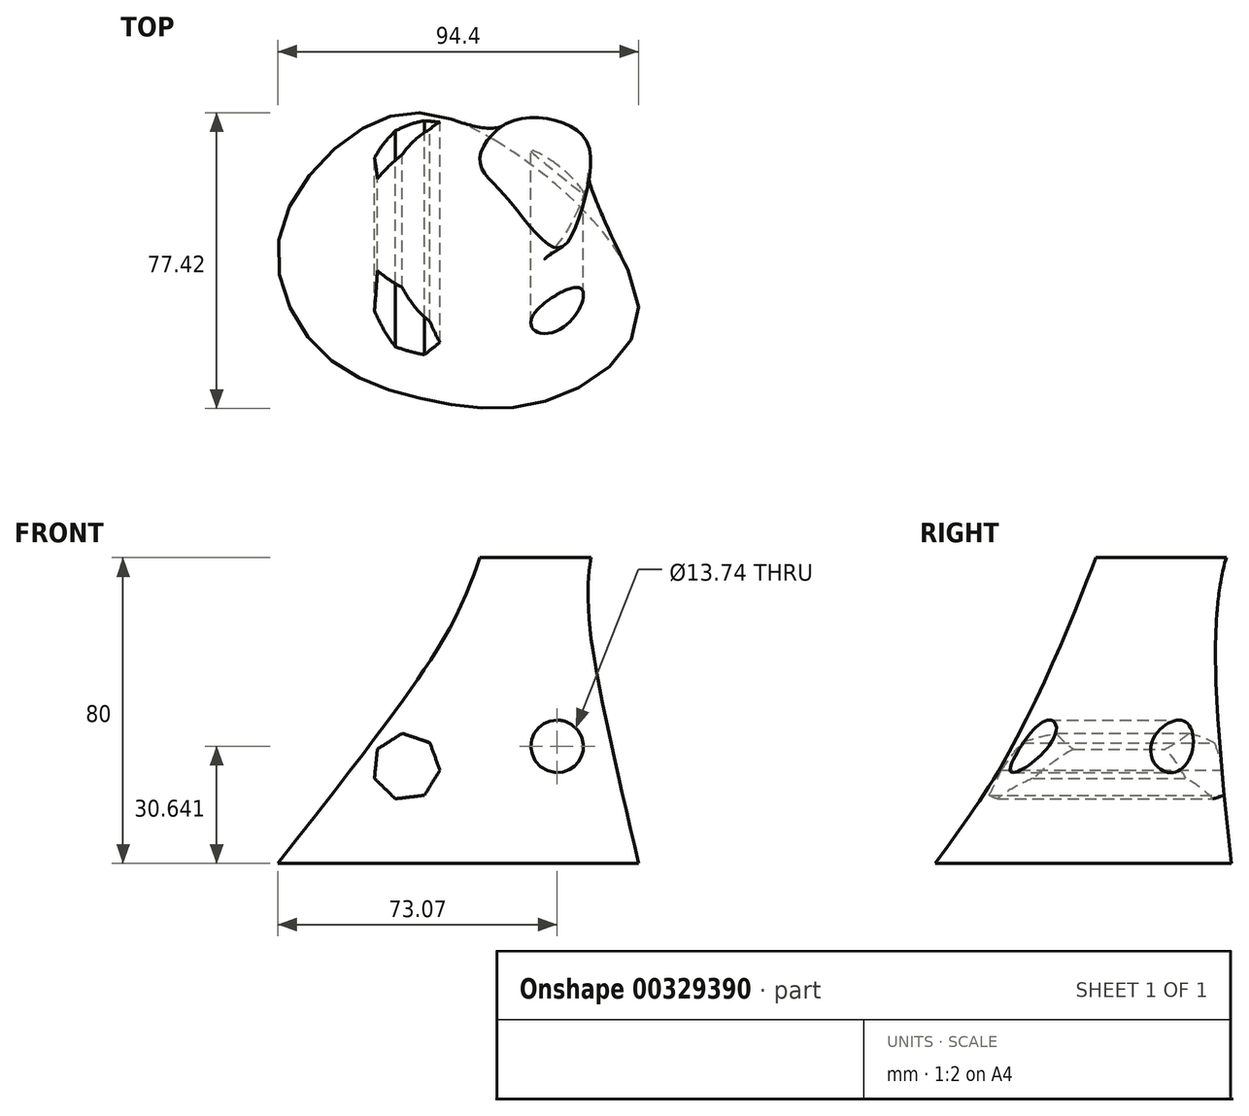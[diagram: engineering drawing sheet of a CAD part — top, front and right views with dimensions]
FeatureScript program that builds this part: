
annotation { "Feature Type Name" : "Feature", "Feature Type Description" : "" }
export const myFeature = defineFeature(function(context is Context, id is Id, definition is map)
    precondition{}
    {
        {
            var Q0;
            Q0=qCreatedBy(makeId("Top.planeOp"),FACE);
            var sketch = newSketch(context, id + "F0", { "sketchPlane" : qUnion([Q0])});
            skFitSpline(sketch, "E0", {"points": [v(0, 0) * mm, v(-43.2, 46.69) * mm, v(-71.5, 47.2) * mm, v(-94.03, 17.95) * mm, v(-81.67, -12.84) * mm, v(-53.17, -24.68) * mm, v(-23.3, -24.29) * mm, v(0, 0) * mm]});
            skSolve(sketch);
        }
        {
            var Q0;
            Q0=qCreatedBy(makeId("Top.planeOp"),FACE);
            cPlane(context, id + "F1", {"entities" : qUnion([Q0]), "cplaneType" : CPlaneType.OFFSET, "offset" : 80 * mm, "width" : 150 * mm, "height" : 150 * mm});
        }
        {
            var Q0;
            Q0=qCreatedBy(id+"F1.planeOp",FACE);
            var sketch = newSketch(context, id + "F2", { "sketchPlane" : qUnion([Q0])});
            skFitSpline(sketch, "E1", {"points": [v(-34.78, 47.94) * mm, v(-41.58, 38.52) * mm, v(-35.15, 29.3) * mm, v(-21.33, 15.5) * mm, v(-15.36, 24.15) * mm, v(-13.2, 42.44) * mm, v(-21.61, 48.78) * mm, v(-34.78, 47.94) * mm]});
            skSolve(sketch);
        }
        {
            var Q0;
            Q0=makeQuery(id+"F2.imprint","IMPRINT",FACE,{"disambiguationData":[TD([[makeQuery(id+"F2.imprint","IMPRINT",EDGE,{"derivedFrom":sQuery(id+"F2.wireOp",EDGE,"E1")}),1.0]])]});
            var Q1;
            Q1=makeQuery(id+"F0.imprint","IMPRINT",FACE,{"disambiguationData":[TD([[makeQuery(id+"F0.imprint","IMPRINT",EDGE,{"derivedFrom":sQuery(id+"F0.wireOp",EDGE,"E0")}),1.0]])]});
            loft(context, id + "F3", {"sheetProfilesArray" : [{ "sheetProfileEntities" : qUnion([Q0]) }, { "sheetProfileEntities" : qUnion([Q1]) }]});
        }
        {
            var Q0;
            Q0=qCreatedBy(makeId("Front.planeOp"),FACE);
            var sketch = newSketch(context, id + "F4", { "sketchPlane" : qUnion([Q0])});
            skCircle(sketch, "E2", {"center": v(-21.32, 30.64) * mm, "radius": 6.87 * mm});
            skCircle(sketch, "E3.cCircle", {"center": v(-60.81, 25.28) * mm, "radius": 7.96 * mm, "construction": true});
            skLineSegment(sketch, "E3.0", {"start": v(-52.02, 24.37) * mm, "end": v(-56.04, 17.84) * mm});
            skLineSegment(sketch, "E3.1", {"start": v(-56.04, 17.84) * mm, "end": v(-63.65, 16.9) * mm});
            skLineSegment(sketch, "E3.2", {"start": v(-63.65, 16.9) * mm, "end": v(-69.13, 22.28) * mm});
            skLineSegment(sketch, "E3.3", {"start": v(-69.13, 22.28) * mm, "end": v(-68.34, 29.9) * mm});
            skLineSegment(sketch, "E3.4", {"start": v(-68.34, 29.9) * mm, "end": v(-61.88, 34.05) * mm});
            skLineSegment(sketch, "E3.5", {"start": v(-61.88, 34.05) * mm, "end": v(-54.62, 31.59) * mm});
            skLineSegment(sketch, "E3.6", {"start": v(-54.62, 31.59) * mm, "end": v(-52.02, 24.37) * mm});
            skPoint(sketch, "E3.0.midPoint", {"position": v(-54.03, 21.1) * mm});
            skCircle(sketch, "E4", {"center": v(-43.08, 33.8) * mm, "radius": 3.52 * mm});
            skSolve(sketch);
        }
        {
            var Q0;
            Q0=makeQuery(id+"F4.imprint","IMPRINT",FACE,{"disambiguationData":[TD([[makeQuery(id+"F4.imprint","IMPRINT",EDGE,{"derivedFrom":sQuery(id+"F4.wireOp",EDGE,"E2")}),1.0]])]});
            var Q1;
            Q1=makeQuery(id+"F4.imprint","IMPRINT",FACE,{"disambiguationData":[TD([[makeQuery(id+"F4.imprint","IMPRINT",EDGE,{"derivedFrom":sQuery(id+"F4.wireOp",EDGE,"E3.0")}),-1.0]])]});
            extrude(context, id + "F5", {"entities" : qUnion([Q0, Q1]), "operationType" : NewBodyOperationType.REMOVE, "depth" : 69 * mm, "hasSecondDirection" : true, "secondDirectionOppositeDirection" : true, "secondDirectionDepth" : 92.1 * mm});
        }
    });
